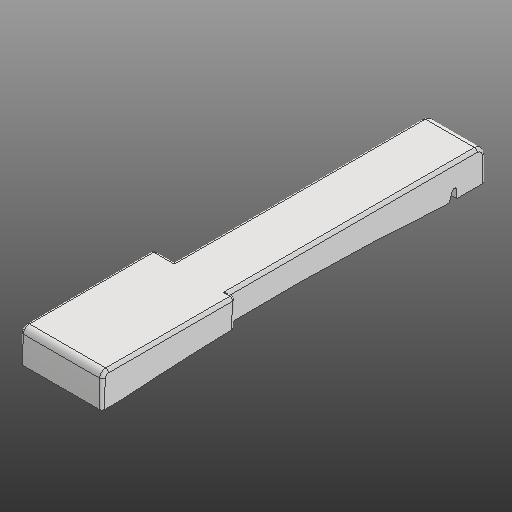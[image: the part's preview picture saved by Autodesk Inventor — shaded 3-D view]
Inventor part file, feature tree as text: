
AUTODESK INVENTOR PART (.ipt)
format: ipt  version: 2020 (Build 240168000, 168)  size: 331,264 bytes
history: native  units: in
note: dims shown in document units (in); Inventor stores cm internally (conversion verified against a paired STEP export)
features: extrude x4, other x3, fillet x2
ambient origin geometry x8: Origin, YZ Plane, XZ Plane, XY Plane, X Axis, Y Axis, Z Axis, Center Point
bodies: Solid1 (feature_tree)
feature tree (9):
  other  "Slot Start Plane"
  other  "Key Profile"
  extrude  "Upper (u)"  TaperAngle=0.0deg  [1 undecoded]
  extrude  "Lower (d)"  TaperAngle=0.0deg  [1 undecoded]
  extrude  "Protrusion Cutout"  Depth=0.0591in
  fillet  "Front Fillet"  Radius=0.1374in
  extrude  "Slot"  [1 undecoded]
  fillet  "Edge Softening"  Radius=0.0787in
  other  "Slot Sketch"
note: 3 required parameter values undecoded (feature->parameter linkage not recoverable at this tier; creation-order binding heuristic only, values carry confidence <= 0.55)
